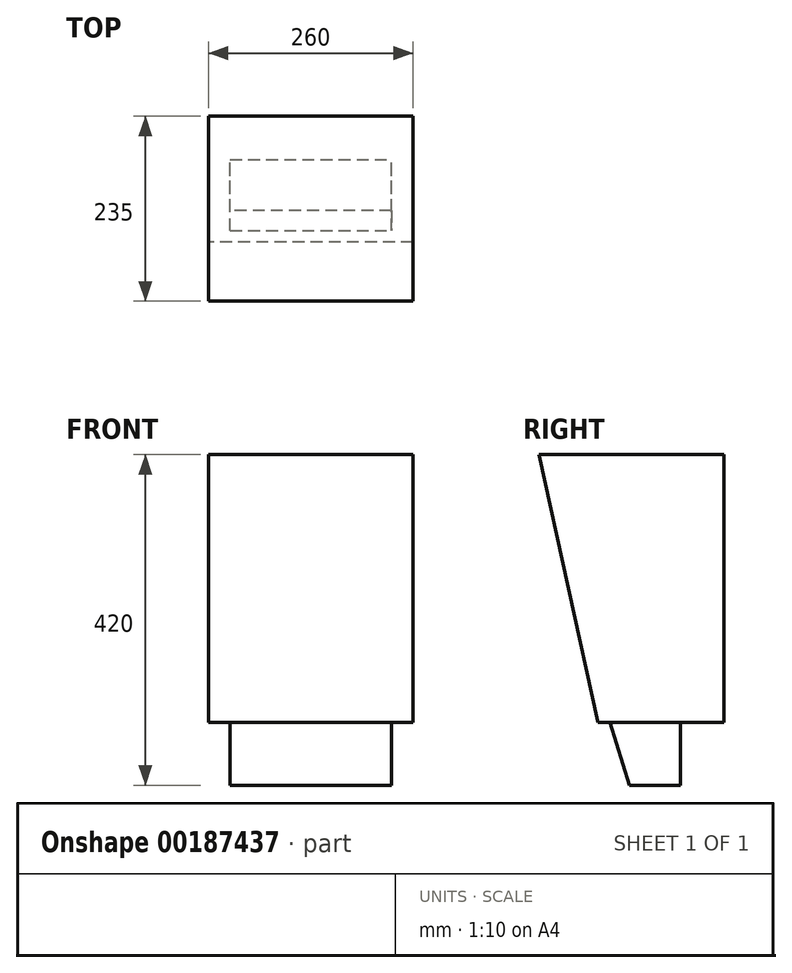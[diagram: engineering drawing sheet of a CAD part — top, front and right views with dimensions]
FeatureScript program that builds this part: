
annotation { "Feature Type Name" : "Feature", "Feature Type Description" : "" }
export const myFeature = defineFeature(function(context is Context, id is Id, definition is map)
    precondition{}
    {
        {
            var Q0;
            Q0=qCreatedBy(makeId("Right.planeOp"),FACE);
            var sketch = newSketch(context, id + "F0", { "sketchPlane" : qUnion([Q0])});
            skLineSegment(sketch, "E0.bottom", {"start": v(-117.5, 170) * mm, "end": v(117.5, 170) * mm});
            skLineSegment(sketch, "E0.top", {"start": v(-117.5, -170) * mm, "end": v(117.5, -170) * mm});
            skLineSegment(sketch, "E0.left", {"start": v(-117.5, 170) * mm, "end": v(-117.5, -170) * mm});
            skLineSegment(sketch, "E0.right", {"start": v(117.5, 170) * mm, "end": v(117.5, -170) * mm});
            skPoint(sketch, "E0.middle", {"position": v(0, 0) * mm});
            skLineSegment(sketch, "E1", {"start": v(-117.5, 170) * mm, "end": v(-42.5, -170) * mm});
            skSolve(sketch);
        }
        {
            var Q0;
            Q0=makeQuery(id+"F0.imprint","IMPRINT",FACE,{"disambiguationData":[TD([[makeQuery(id+"F0.imprint","IMPRINT",EDGE,{"derivedFrom":sQuery(id+"F0.wireOp",EDGE,"E0.bottom")}),-1.0]])]});
            extrude(context, id + "F1", {"entities" : qUnion([Q0]), "endBound" : BoundingType.SYMMETRIC, "depth" : 260 * mm, "offsetDistance" : 25 * mm});
        }
        {
            var Q0;
            Q0=makeQuery(id+"F1.opExtrude","SWEPT_FACE",FACE,{"disambiguationData":[OSD([sQuery(id+"F0.wireOp",EDGE,"E0.top")])]});
            var sketch = newSketch(context, id + "F2", { "sketchPlane" : qUnion([Q0])});
            skLineSegment(sketch, "E2.bottom", {"start": v(-102.5, 27.5) * mm, "end": v(102.5, 27.5) * mm});
            skLineSegment(sketch, "E2.top", {"start": v(-102.5, -62.5) * mm, "end": v(102.5, -62.5) * mm});
            skLineSegment(sketch, "E2.left", {"start": v(-102.5, 27.5) * mm, "end": v(-102.5, -62.5) * mm});
            skLineSegment(sketch, "E2.right", {"start": v(102.5, 27.5) * mm, "end": v(102.5, -62.5) * mm});
            skSolve(sketch);
        }
        {
            var Q0;
            Q0 = qSketchRegion(id + "F2", true);
            extrude(context, id + "F3", {"entities" : qUnion([Q0]), "operationType" : NewBodyOperationType.ADD, "depth" : 80 * mm, "offsetDistance" : 25 * mm});
        }
        {
            var Q0;
            Q0=makeQuery(id+"F3.opExtrude","SWEPT_FACE",FACE,{"disambiguationData":[OSD([sQuery(id+"F2.wireOp",EDGE,"E2.left")])]});
            var sketch = newSketch(context, id + "F4", { "sketchPlane" : qUnion([Q0])});
            skLineSegment(sketch, "E3", {"start": v(27.5, -170) * mm, "end": v(2.5, -250) * mm});
            skSolve(sketch);
        }
        {
            var Q0;
            Q0 = qSketchRegion(id + "F4", true);
            var Q1;
            {var subQ0=sQuery(id+"F4.wireOp",EDGE,"E3");Q1=makeQuery(id+"F4.imprint","IMPRINT",FACE,{"disambiguationData":[TD([[makeQuery(id+"F4.imprint","IMPRINT",EDGE,{"derivedFrom":subQ0}),1.0]])]});}
            extrude(context, id + "F5", {"entities" : qUnion([Q0, Q1]), "operationType" : NewBodyOperationType.REMOVE, "endBound" : BoundingType.THROUGH_ALL, "oppositeDirection" : true, "depth" : 25 * mm, "offsetDistance" : 25 * mm});
        }
    });
